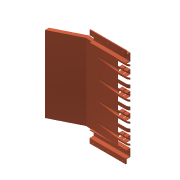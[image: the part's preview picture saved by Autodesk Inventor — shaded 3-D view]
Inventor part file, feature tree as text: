
AUTODESK INVENTOR PART (.ipt)
format: ipt  version: 2015 (Build 190159000, 159)  size: 557,056 bytes
history: native  units: mm
features: sketch x15, extrude x14, pattern_linear x6, other x3, revolve x1
ambient origin geometry x8: Origin, YZ Plane, XZ Plane, XY Plane, X Axis, Y Axis, Z Axis, Center Point
bodies: 实体1 (feature_tree)
feature tree (39):
  extrude  "拉伸1"  Depth=15.12mm
  extrude  "拉伸2"  Depth=2.0mm
  extrude  "拉伸3"  Depth=20.0mm
  pattern_linear  "矩形阵列1"  Count1=6  [1 undecoded]
  extrude  "拉伸4"  Depth=480.0mm TaperAngle=0.0deg
  extrude  "拉伸5"  Depth=20.0mm
  pattern_linear  "矩形阵列2"  Count1=4  [1 undecoded]
  extrude  "拉伸6"  Depth=81.504mm
  extrude  "拉伸8"  Depth=10.0mm
  extrude  "拉伸9"  Depth=10.0mm
  pattern_linear  "矩形阵列3"  Count1=3  [1 undecoded]
  extrude  "拉伸10"  Depth=10.0mm
  pattern_linear  "矩形阵列4"  Count1=5 Spacing1=0.0mm
  extrude  "拉伸11"  Depth=20.0mm
  extrude  "拉伸12"  Depth=50.0mm TaperAngle=0.0deg
  other  "工作轴1"
  revolve  "旋转1"  [1 undecoded]
  extrude  "拉伸13"  Depth=4.0mm
  extrude  "拉伸14"  Depth=4.0mm
  pattern_linear  "矩形阵列5"  Spacing1=4.0mm  [1 undecoded]
  extrude  "拉伸15"  Depth=4.0mm
  pattern_linear  "矩形阵列6"  Count1=4  [1 undecoded]
  other  "加厚1"
  other  "加厚2"
  sketch  "草图1"  dims[d0=3.335281mm d1=15.12mm]
  sketch  "草图2"  dims[d2=2.0mm d3=213.363mm]
  sketch  "草图3"  dims[d4=480.0mm d5=0.0mm d6=20.0mm d7=60.0mm]
  sketch  "草图4"  dims[d8=2.0mm d9=480.0mm d10=0.0mm]
  sketch  "草图5"  dims[d11=20.0mm d12=20.0mm]
  sketch  "草图6"  dims[d13=0.0mm d14=40.0mm d16=120.0mm]
  sketch  "草图8"  dims[d17=164.137mm d18=81.504mm]
  sketch  "草图9"  dims[d19=480.0mm d20=0.0mm d21=10.0mm]
  sketch  "草图10"  dims[d22=2.005016mm d23=10.0mm d24=30.0mm]
  sketch  "草图11"  dims[d25=2.0mm d26=10.0mm]
  sketch  "草图12"  dims[d27=2.0mm d28=50.0mm d29=0.0mm]
  sketch  "草图13"  dims[d30=40.0mm d32=120.0mm d33=20.0mm]
  sketch  "草图14"  dims[d34=110.0mm d35=50.0mm d36=0.0mm]
  sketch  "草图15"  dims[d42=10.0mm d43=10.0mm]
  sketch  "草图16"  dims[d44=50.0mm d45=0.0mm d46=4.0mm d47=4.0mm d48=4.0mm d49=4.0mm d50=40.0mm d51=30.0mm d52=2.5mm d53=4.0mm d54=4.0mm d55=4.0mm d56=4.0mm d57=40.0mm d58=2.5mm d59=30.0mm d60=227.5mm d61=0.0mm d62=30.0mm d64=120.0mm d65=20.0mm d66=20.0mm d67=4.0mm d68=0.0mm d69=20.0mm d71=476.0mm d72=8.0mm d73=8.0mm d74=8.0mm d75=8.0mm d76=8.0mm d77=8.0mm d78=13.0mm d79=20.0mm d80=13.0mm d81=13.0mm d82=20.0mm d83=113.75mm d84=20.0mm d85=13.0mm d86=13.0mm d87=13.0mm d88=113.75mm d89=20.0mm d90=4.0mm d91=0.0mm d92=2.5mm d93=7.0mm d94=20.0mm d95=25.0mm d96=13.0mm d97=10.0mm d98=0.0mm d99=10.0mm d100=20.0mm d101=10.0mm d102=2.005016mm d103=45.0deg d104=10.0mm d105=480.0mm d106=0.0mm d107=4.0mm d108=0.0mm d109=20.0mm d111=476.0mm d112=5.0mm d113=5.0mm d114=5.0mm d115=14.0mm d116=7.5mm d117=7.5mm d118=4.0mm d119=0.0mm d120=20.0mm d122=476.0mm d123=1.704mm d124=1.704mm d125=1.704mm d126=1.704mm]
note: 6 required parameter values undecoded (feature->parameter linkage not recoverable at this tier; creation-order binding heuristic only, values carry confidence <= 0.55)